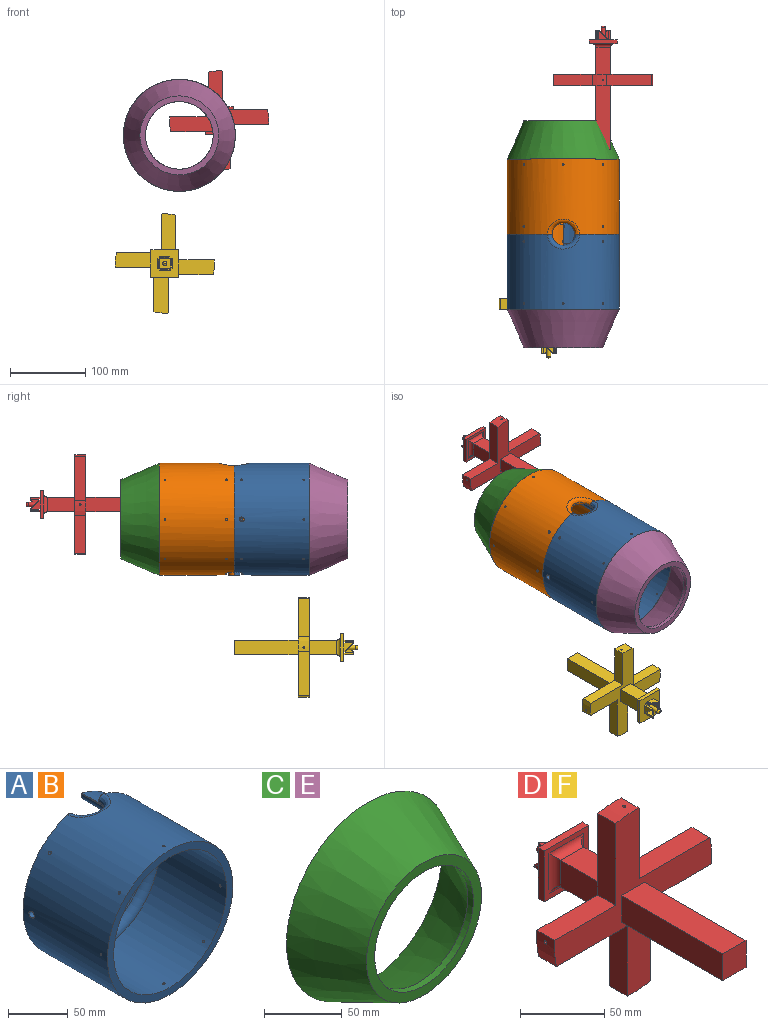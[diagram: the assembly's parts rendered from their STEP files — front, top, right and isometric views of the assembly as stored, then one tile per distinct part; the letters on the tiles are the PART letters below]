
ASSEMBLY  parts=6 mates=2
PART A: 46 faces, bbox 152.8x120x154.6 mm
  f0: plane 50x25mm, normal (0,0,-1), area 720.9mm2, adj f3,f18,f39,f40,f41,f42,f43,f44
  f1: cylinder r=74.5mm len=149mm, axis (0,-1,0), area 45198.5mm2, adj f2,f3,f6,f7,f8,f9,f10,f11
  f2: cylinder r=74.5mm len=8.9mm, axis (0,-1,0), area 8.9mm2, adj f1,f39
  f3: plane 149x146.56mm, normal (0,1,0), area 3009.1mm2, adj f0,f1,f5,f21,f22,f27,f42,f43
  f4: plane 8.5x7.5mm, normal (-1,0,0), area 63.8mm2, adj f23,f26,f27,f33
  f5: cylinder r=67mm len=134mm, axis (0,-1,0), area 37757.7mm2, adj f3,f6,f7,f8,f9,f10,f11,f12
  f6: plane 149x149mm, normal (0,-1,0), area 3334mm2, adj f1,f5
  f7: cylinder r=1.05mm len=7.5mm, axis (0,0,1), area 49.5mm2, adj f1,f5
  f8: cylinder r=1.05mm len=7.5mm, axis (0,0,1), area 49.5mm2, adj f1,f5
  f9: cylinder r=1.05mm len=6.79mm, axis (-0.71,0,0.71), area 49.5mm2, adj f1,f5
  f10: cylinder r=1.05mm len=6.79mm, axis (-0.71,0,0.71), area 49.5mm2, adj f1,f5
  f11: cylinder r=1.05mm len=7.5mm, axis (-1,0,0), area 49.5mm2, adj f1,f5
  f12: cylinder r=1.05mm len=7.5mm, axis (-1,0,0), area 49.5mm2, adj f1,f5
  f13: cylinder r=1.05mm len=6.79mm, axis (-0.71,0,-0.71), area 49.5mm2, adj f1,f5
  f14: cylinder r=1.05mm len=6.79mm, axis (-0.71,0,-0.71), area 49.5mm2, adj f1,f5
  f15: cylinder r=1.5mm len=7.5mm, axis (1,0,0), area 70.7mm2, adj f1,f31
  f16: cylinder r=1.5mm len=7.43mm, axis (0.71,0,-0.71), area 70.7mm2, adj f1,f30
  f17: cylinder r=1.5mm len=7.43mm, axis (0.71,0,-0.71), area 70.7mm2, adj f1,f5
  f18: cylinder r=1.5mm len=3mm, axis (0,0,-1), area 28.3mm2, adj f0,f5,f28
  f19: cylinder r=1.5mm len=7.43mm, axis (-0.71,0,-0.71), area 70.7mm2, adj f1,f5
  f20: cylinder r=1.5mm len=7.43mm, axis (-0.71,0,-0.71), area 70.7mm2, adj f1,f29
  f21: cylinder r=15mm len=30mm, axis (0,0,-1), area 88.9mm2, adj f3,f5,f22
  f22: bspline ~42.89x21.74mm, area 463.4mm2, adj f1,f3,f21
  f23: plane 132.3x67mm, normal (0,1,0), area 1373mm2, adj f4,f25,f26,f27,f37
  f24: plane 28.5x7.5mm, normal (-1,0,0), area 201.7mm2, adj f5,f26,f27,f28,f33,f36
  f25: plane 40x0.56mm, normal (-0.98,0,0.2), area 23mm2, adj f5,f23,f27,f36,f37
  f26: cylinder r=59.5mm len=115.63mm, axis (0,-1,0), area 5396.3mm2, adj f4,f23,f24,f32,f33,f34,f35,f36
  f27: cylinder r=67mm len=132.3mm, axis (0,-1,0), area 3882.3mm2, adj f3,f4,f23,f24,f25,f32,f33,f34
  f28: cylinder r=67mm len=3mm, axis (0,-1,0), area 3.5mm2, adj f18,f24
  f29: cylinder r=67mm len=3mm, axis (0,-1,0), area 7.1mm2, adj f20
  f30: cylinder r=67mm len=3mm, axis (0,-1,0), area 7.1mm2, adj f16
  f31: cylinder r=67mm len=3mm, axis (0,-1,0), area 7.1mm2, adj f15
  f32: cylinder r=1.5mm len=7.43mm, axis (0.71,0,-0.71), area 70.7mm2, adj f26,f27
  f33: cylinder r=1.5mm len=7.5mm, axis (0,0,-1), area 35.3mm2, adj f4,f24,f26,f27
  f34: cylinder r=1.5mm len=7.43mm, axis (-0.71,0,-0.71), area 70.7mm2, adj f26,f27
  f35: cylinder r=1.5mm len=7.5mm, axis (-1,0,0), area 70.7mm2, adj f26,f27
  f36: torus R=67mm, axis (0,1,0), area 2109.8mm2, adj f5,f24,f25,f26,f37
  f37: cylinder r=7.5mm len=39.98mm, axis (0,-1,0), area 400.9mm2, adj f23,f25,f26,f36
  f38: cylinder r=3.17mm len=7.51mm, axis (1,0,0), area 149mm2, adj f1,f5
  f39: cylinder r=7.5mm len=11.95mm, axis (0,0,-1), area 65.4mm2, adj f0,f1,f2,f40,f43
  f40: cylinder r=25mm len=23.28mm, axis (0,0,-1), area 101.4mm2, adj f0,f1,f39,f41
  f41: cylinder r=7.5mm len=11.95mm, axis (0,0,-1), area 65.4mm2, adj f0,f1,f40,f42
  f42: cylinder r=25mm len=11.64mm, axis (0,0,-1), area 6.2mm2, adj f0,f1,f3,f41
  f43: cylinder r=25mm len=11.64mm, axis (0,0,-1), area 6.2mm2, adj f0,f1,f3,f39
  f44: cylinder r=7.5mm len=15mm, axis (0,0,-1), area 117.8mm2, adj f0,f3,f45
  f45: plane 15x7.5mm, normal (0,0,-1), area 88.4mm2, adj f3,f44
PART B: same geometry as A
PART C: 5 faces, bbox 149x51x149 mm
  f0: cone r=52.5mm half-angle=23.3deg, axis (0,1,0), area 22160.6mm2, adj f2,f4
  f1: cone r=67mm half-angle=25.7deg, axis (0,1,0), area 17851.1mm2, adj f2,f3
  f2: cone r=74.5mm half-angle=87.8deg, axis (0,1,0), area 3336.4mm2, adj f0,f1
  f3: cylinder r=45mm len=90mm, axis (0,1,0), area 1413.7mm2, adj f1,f4
  f4: plane 105x105mm, normal (0,-1,0), area 2297.3mm2, adj f0,f3
PART D: 68 faces, bbox 132x164.5x132 mm
  f0: cylinder r=1.05mm len=65.99mm, axis (1,0,0), area 431mm2, adj f58,f66,f67
  f1: plane 59.34x15mm, normal (1,0,0), area 890.2mm2, adj f5,f6,f57,f64
  f2: plane 59.34x15mm, normal (0,0,-1), area 890.2mm2, adj f5,f6,f59,f63
  f3: plane 59.34x15mm, normal (-1,0,0), area 890.2mm2, adj f5,f6,f60,f62
  f4: plane 59.34x15mm, normal (0,0,1), area 890.2mm2, adj f5,f6,f58,f61
  f5: plane 132x132mm, normal (0,-1,0), area 4495.2mm2, adj f1,f2,f3,f4,f12,f13,f14,f15
  f6: plane 132x132mm, normal (0,1,0), area 4495.2mm2, adj f1,f2,f3,f4,f7,f8,f9,f10
  f7: plane 36x19.38mm, normal (-1,0,0), area 697.6mm2, adj f6,f8,f9,f18
  f8: plane 36x19.38mm, normal (0,0,1), area 697.6mm2, adj f6,f7,f10,f20
  f9: plane 36x19.38mm, normal (0,0,-1), area 697.6mm2, adj f6,f7,f10,f17
  f10: plane 36x19.38mm, normal (1,0,0), area 697.6mm2, adj f6,f8,f9,f19
  f11: plane 37x37mm, normal (0,-1,0), area 505.9mm2, adj f17,f18,f19,f20,f21,f22,f23,f24
  f12: plane 85x19.38mm, normal (-1,0,0), area 1647.2mm2, adj f5,f13,f15,f16
  f13: plane 85x19.38mm, normal (0,0,-1), area 1647.2mm2, adj f5,f12,f14,f16
  f14: plane 85x19.38mm, normal (1,0,0), area 1647.2mm2, adj f5,f13,f15,f16
  f15: plane 85x19.38mm, normal (0,0,1), area 1647.2mm2, adj f5,f12,f14,f16
  f16: plane 19.38x19.38mm, normal (0,-1,0), area 375.5mm2, adj f12,f13,f14,f15
  f17: cylinder r=5mm len=29.38mm, axis (-1,0,0), area 180.7mm2, adj f9,f11,f18,f19
  f18: cylinder r=5mm len=29.38mm, axis (0,0,1), area 180.7mm2, adj f7,f11,f17,f20
  f19: cylinder r=5mm len=29.38mm, axis (0,0,-1), area 180.7mm2, adj f10,f11,f17,f20
  f20: cylinder r=5mm len=29.38mm, axis (1,0,0), area 180.7mm2, adj f8,f11,f18,f19
  f21: plane 37x5mm, normal (0,0,-1), area 185mm2, adj f11,f22,f24,f56
  f22: plane 37x5mm, normal (1,0,0), area 185mm2, adj f11,f21,f23,f56
  f23: plane 37x5mm, normal (0,0,1), area 185mm2, adj f11,f22,f24,f56
  f24: plane 37x5mm, normal (-1,0,0), area 185mm2, adj f11,f21,f23,f56
  f25: plane 0.75x0.75mm, normal (0,1,0), area 0.4mm2, adj f26
  f26: torus R=0.38mm, axis (0,-1,0), area 48.5mm2, adj f25,f31
  f27: cylinder r=1mm len=2.54mm, axis (-1,0,0), area 4.9mm2, adj f32,f33,f34,f35,f36,f37
  f28: cylinder r=1mm len=2.54mm, axis (0,0,1), area 4.9mm2, adj f38,f39,f40,f41,f42,f43
  f29: cylinder r=1mm len=2.54mm, axis (0,0,1), area 4.9mm2, adj f44,f45,f46,f47,f48,f49
  f30: cylinder r=1mm len=2.54mm, axis (1,0,0), area 4.9mm2, adj f50,f51,f52,f53,f54,f55
  f31: cylinder r=2.88mm len=15.98mm, axis (0,1,0), area 288.6mm2, adj f26,f56
  f32: cylinder r=1mm len=13.76mm, axis (0,0.72,0.69), area 27.4mm2, adj f27,f33,f37,f56
  f33: plane 12.34x11.92mm, normal (0,0.69,-0.72), area 9.2mm2, adj f27,f32,f34,f56
  f34: cylinder r=1mm len=13.76mm, axis (0,-0.72,-0.69), area 27.4mm2, adj f27,f33,f35,f56
  f35: plane 12.37x12.25mm, normal (-1,0,0), area 77.6mm2, adj f27,f34,f36,f56
  f36: plane 11.65x2.54mm, normal (0,0,1), area 29.6mm2, adj f27,f35,f37,f56
  f37: plane 12.37x12.25mm, normal (1,0,0), area 77.6mm2, adj f27,f32,f36,f56
  f38: cylinder r=1mm len=13.76mm, axis (0.69,0.72,0), area 27.4mm2, adj f28,f39,f43,f56
  f39: plane 12.34x11.92mm, normal (-0.72,0.69,0), area 9.2mm2, adj f28,f38,f40,f56
  f40: cylinder r=1mm len=13.76mm, axis (-0.69,-0.72,0), area 27.4mm2, adj f28,f39,f41,f56
  f41: plane 12.37x12.25mm, normal (0,0,1), area 77.6mm2, adj f28,f40,f42,f56
  f42: plane 11.65x2.54mm, normal (1,0,0), area 29.6mm2, adj f28,f41,f43,f56
  f43: plane 12.37x12.25mm, normal (0,0,-1), area 77.6mm2, adj f28,f38,f42,f56
  f44: plane 12.37x12.25mm, normal (0,0,-1), area 77.6mm2, adj f29,f45,f49,f56
  f45: plane 11.65x2.54mm, normal (-1,0,0), area 29.6mm2, adj f29,f44,f46,f56
  f46: plane 12.37x12.25mm, normal (0,0,1), area 77.6mm2, adj f29,f45,f47,f56
  f47: cylinder r=1mm len=13.76mm, axis (0.69,-0.72,0), area 27.4mm2, adj f29,f46,f48,f56
  f48: plane 12.34x11.92mm, normal (0.72,0.69,0), area 9.2mm2, adj f29,f47,f49,f56
  f49: cylinder r=1mm len=13.76mm, axis (0.69,-0.72,0), area 27.4mm2, adj f29,f44,f48,f56
  f50: plane 12.34x11.92mm, normal (0,0.69,0.72), area 9.2mm2, adj f30,f51,f55,f56
  f51: cylinder r=1mm len=13.76mm, axis (0,-0.72,0.69), area 27.4mm2, adj f30,f50,f52,f56
  f52: plane 12.37x12.25mm, normal (1,0,0), area 77.6mm2, adj f30,f51,f53,f56
  f53: plane 11.65x2.54mm, normal (0,0,-1), area 29.6mm2, adj f30,f52,f54,f56
  f54: plane 12.37x12.25mm, normal (-1,0,0), area 77.6mm2, adj f30,f53,f55,f56
  f55: cylinder r=1mm len=13.76mm, axis (0,-0.72,0.69), area 27.4mm2, adj f30,f50,f54,f56
  f56: plane 37x37mm, normal (0,1,0), area 1206.9mm2, adj f21,f22,f23,f24,f31,f32,f33,f34
  f57: cylinder r=66mm len=19.69mm, axis (0,-1,0), area 293.8mm2, adj f1,f5,f6,f63,f66
  f58: cylinder r=66mm len=19.69mm, axis (0,-1,0), area 293.8mm2, adj f0,f4,f5,f6,f64
  f59: cylinder r=66mm len=19.69mm, axis (0,-1,0), area 293.8mm2, adj f2,f5,f6,f62,f65
  f60: cylinder r=66mm len=19.69mm, axis (0,-1,0), area 293.8mm2, adj f3,f5,f6,f61,f67
  f61: plane 51.12x15mm, normal (1,0,0), area 766.8mm2, adj f4,f5,f6,f60
  f62: plane 51.12x15mm, normal (0,0,1), area 766.8mm2, adj f3,f5,f6,f59
  f63: plane 51.12x15mm, normal (-1,0,0), area 766.8mm2, adj f2,f5,f6,f57
  f64: plane 51.12x15mm, normal (0,0,-1), area 766.8mm2, adj f1,f5,f6,f58
  f65: cylinder r=1.05mm len=65.99mm, axis (1,0,0), area 431mm2, adj f59,f66,f67
  f66: cylinder r=1.05mm len=65.99mm, axis (0,0,-1), area 431mm2, adj f0,f57,f65
  f67: cylinder r=1.05mm len=65.99mm, axis (0,0,-1), area 431mm2, adj f0,f60,f65
PART E: same geometry as C
PART F: same geometry as D
PLACE A t=(-102.93,-311.48,67.17)mm
PLACE B rot(axis=(0,0,-1),180deg) t=(-102.93,-19.63,67.17)mm
PLACE C rot(axis=(0,0,-1),180deg) t=(-102.93,-19.63,67.17)mm
PLACE D t=(-49.94,111.38,86.96)mm
PLACE E t=(-102.93,-311.48,67.17)mm
PLACE F rot(axis=(1,0,0),180deg) t=(-122.23,-329.96,-103.28)mm
MATE planar F.f26 <-> E.f0  axis (0,-1,0) through (-122.23,-311.48,-103.28)mm
MATE cylindrical A.f1 <-> B.f1  axis (0,-1,0) through (-102.93,-155.48,67.17)mm
